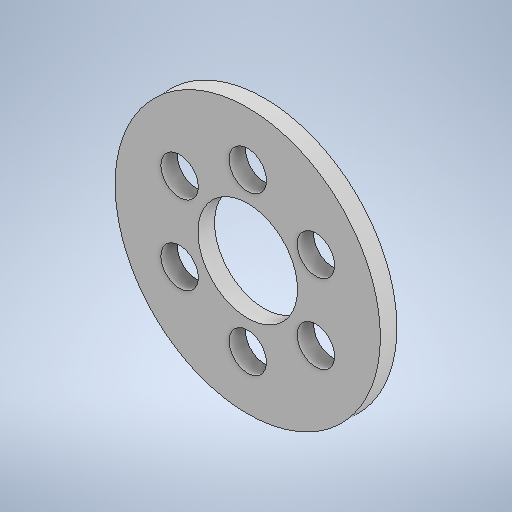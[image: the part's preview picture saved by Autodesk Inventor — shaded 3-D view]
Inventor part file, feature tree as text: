
AUTODESK INVENTOR PART (.ipt)
format: ipt  version: 2025.2 (Build 292293000, 293)  size: 246,272 bytes
history: native  units: mm
features: sketch x2, extrude x1
ambient origin geometry x8: Origin, YZ Plane, XZ Plane, XY Plane, X Axis, Y Axis, Z Axis, Center Point
bodies: Solid1 (feature_tree)
feature tree (3):
  extrude  "Extrusion1"  Depth=19.0mm
  sketch  "Sketch1"  dims[d0=32.0mm d1=19.0mm]
  sketch  "Sketch Circular Pattern1"  dims[d2=4.5mm d3=60.0mm d5=360.0deg d7=12.0mm d8=2.0mm d9=0.0mm]
